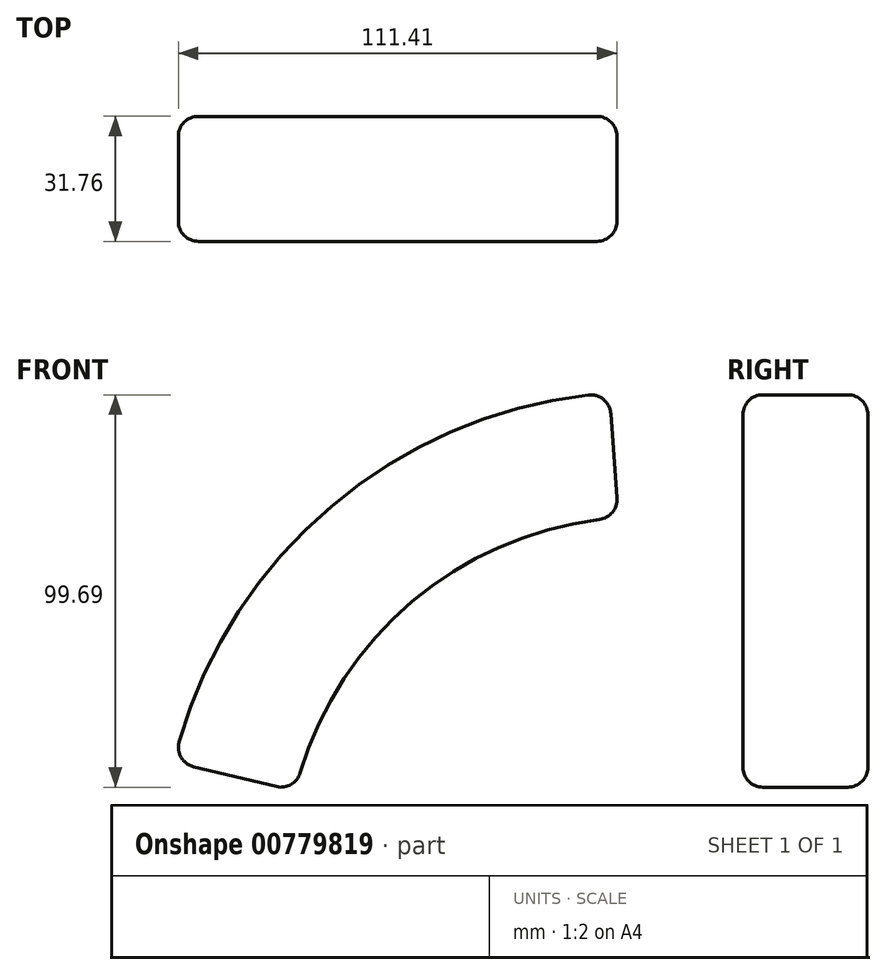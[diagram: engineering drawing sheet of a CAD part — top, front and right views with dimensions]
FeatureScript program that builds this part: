
annotation { "Feature Type Name" : "Feature", "Feature Type Description" : "" }
export const myFeature = defineFeature(function(context is Context, id is Id, definition is map)
    precondition{}
    {
        {
            var Q0;
            Q0=qCreatedBy(makeId("Front.planeOp"),FACE);
            var sketch = newSketch(context, id + "F0", { "sketchPlane" : qUnion([Q0])});
            skArc(sketch, "E0", {"start": v(57.93, 14.66) * mm, "mid": v(5.56, -6.7) * mm, "end": v(-24.1, -54.85) * mm});
            skArc(sketch, "E1.0", {"start": v(55.65, 46.32) * mm, "mid": v(-14.96, 17.52) * mm, "end": v(-54.97, -47.4) * mm});
            skLineSegment(sketch, "E2", {"start": v(-54.97, -47.4) * mm, "end": v(-24.1, -54.85) * mm});
            skLineSegment(sketch, "E3", {"start": v(55.65, 46.32) * mm, "end": v(57.93, 14.66) * mm});
            skSolve(sketch);
        }
        {
            var Q0;
            Q0=makeQuery(id+"F0.imprint","IMPRINT",FACE,{"disambiguationData":[TD([[makeQuery(id+"F0.imprint","IMPRINT",EDGE,{"derivedFrom":sQuery(id+"F0.wireOp",EDGE,"E0")}),-1.0]])]});
            extrude(context, id + "F1", {"entities" : qUnion([Q0]), "endBound" : BoundingType.SYMMETRIC, "depth" : 31.75 * mm, "offsetDistance" : 25.4 * mm});
        }
        {
            var Q0;
            Q0=makeQuery(id+"F1.opExtrude","CAP_EDGE",EDGE,{"disambiguationData":[OSD([sQuery(id+"F0.wireOp",EDGE,"E1.0")])],"isStart":false});
            var Q1;
            Q1=makeQuery(id+"F1.opExtrude","CAP_EDGE",EDGE,{"disambiguationData":[OSD([sQuery(id+"F0.wireOp",EDGE,"E0")])],"isStart":false});
            var Q2;
            Q2=makeQuery(id+"F1.opExtrude","SWEPT_EDGE",EDGE,{"disambiguationData":[OSD([sQuery(id+"F0.wireOp",EDGE,"E0"),sQuery(id+"F0.wireOp",EDGE,"E3")])]});
            var Q3;
            Q3=makeQuery(id+"F1.opExtrude","CAP_EDGE",EDGE,{"disambiguationData":[OSD([sQuery(id+"F0.wireOp",EDGE,"E3")])],"isStart":true});
            var Q4;
            Q4=makeQuery(id+"F1.opExtrude","SWEPT_EDGE",EDGE,{"disambiguationData":[OSD([sQuery(id+"F0.wireOp",EDGE,"E1.0"),sQuery(id+"F0.wireOp",EDGE,"E3")])]});
            var Q5;
            Q5=makeQuery(id+"F1.opExtrude","CAP_EDGE",EDGE,{"disambiguationData":[OSD([sQuery(id+"F0.wireOp",EDGE,"E3")])],"isStart":false});
            var Q6;
            Q6=makeQuery(id+"F1.opExtrude","CAP_EDGE",EDGE,{"disambiguationData":[OSD([sQuery(id+"F0.wireOp",EDGE,"E1.0")])],"isStart":true});
            var Q7;
            Q7=makeQuery(id+"F1.opExtrude","CAP_EDGE",EDGE,{"disambiguationData":[OSD([sQuery(id+"F0.wireOp",EDGE,"E0")])],"isStart":true});
            var Q8;
            Q8=makeQuery(id+"F1.opExtrude","SWEPT_EDGE",EDGE,{"disambiguationData":[OSD([sQuery(id+"F0.wireOp",EDGE,"E0"),sQuery(id+"F0.wireOp",EDGE,"E2")])]});
            var Q9;
            Q9=makeQuery(id+"F1.opExtrude","CAP_EDGE",EDGE,{"disambiguationData":[OSD([sQuery(id+"F0.wireOp",EDGE,"E2")])],"isStart":true});
            var Q10;
            Q10=makeQuery(id+"F1.opExtrude","SWEPT_EDGE",EDGE,{"disambiguationData":[OSD([sQuery(id+"F0.wireOp",EDGE,"E1.0"),sQuery(id+"F0.wireOp",EDGE,"E2")])]});
            var Q11;
            Q11=makeQuery(id+"F1.opExtrude","CAP_EDGE",EDGE,{"disambiguationData":[OSD([sQuery(id+"F0.wireOp",EDGE,"E2")])],"isStart":false});
            fillet(context, id + "F2", {"entities" : qUnion([Q0, Q1, Q2, Q3, Q4, Q5, Q6, Q7, Q8, Q9, Q10, Q11]), "radius" : 5.08 * mm, "tangentPropagation" : true, "allowEdgeOverflow" : false});
        }
    });
